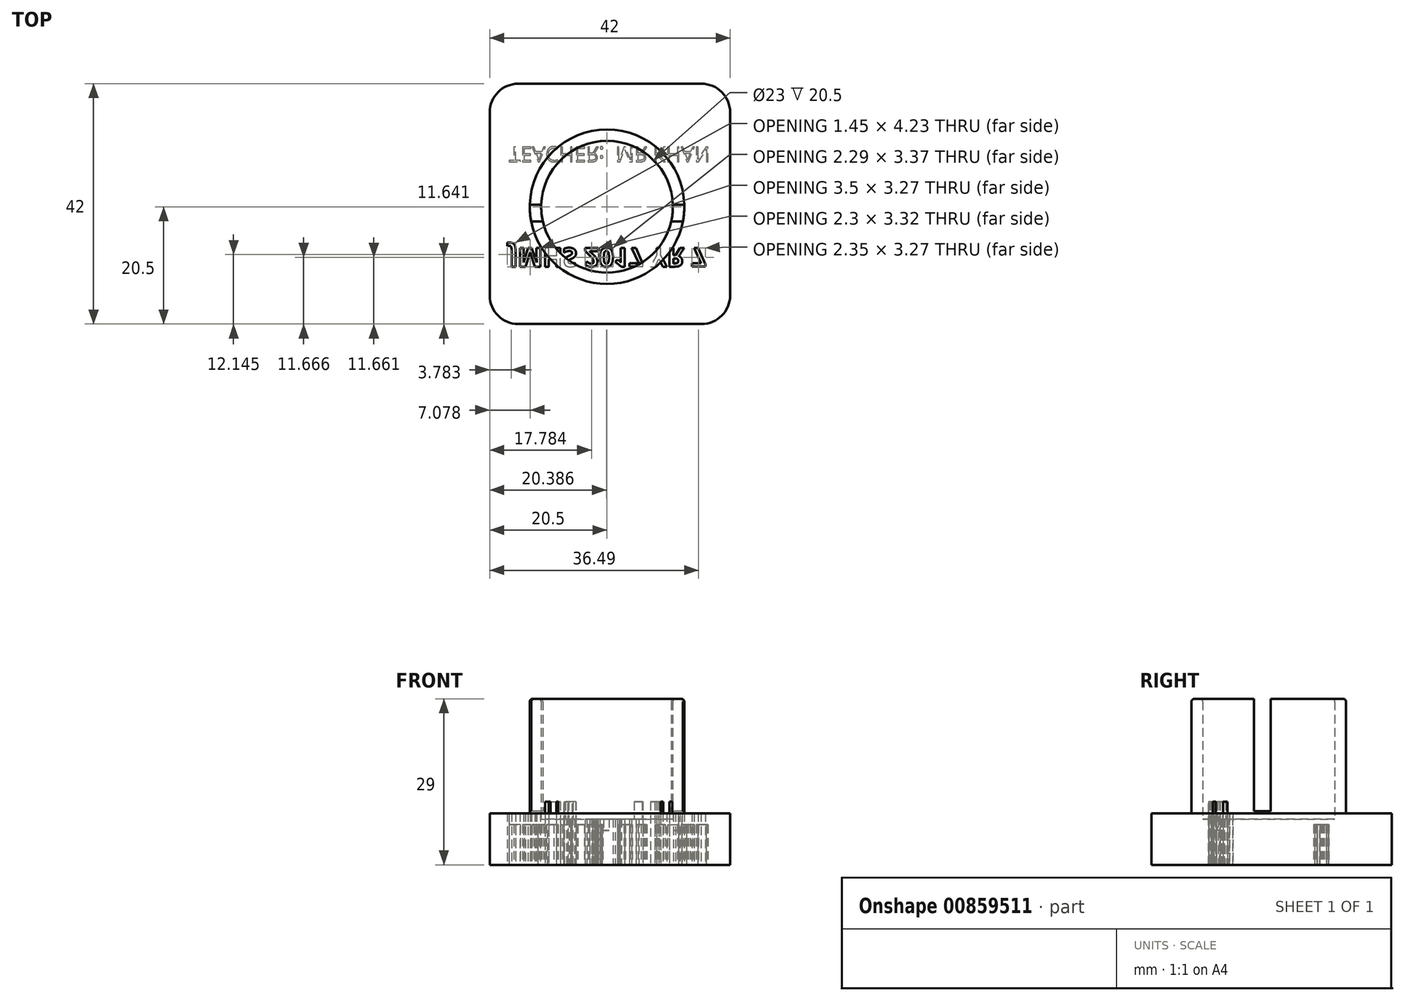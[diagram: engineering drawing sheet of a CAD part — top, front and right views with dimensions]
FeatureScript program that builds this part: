
annotation { "Feature Type Name" : "Feature", "Feature Type Description" : "" }
export const myFeature = defineFeature(function(context is Context, id is Id, definition is map)
    precondition{}
    {
        {
            var Q0;
            Q0=qCreatedBy(makeId("Top.planeOp"),FACE);
            var sketch = newSketch(context, id + "F0", { "sketchPlane" : qUnion([Q0])});
            skLineSegment(sketch, "E0.bottom", {"start": v(5, 0) * mm, "end": v(37, 0) * mm});
            skLineSegment(sketch, "E0.top", {"start": v(5, 42) * mm, "end": v(37, 42) * mm});
            skLineSegment(sketch, "E0.left", {"start": v(0, 5) * mm, "end": v(0, 37) * mm});
            skLineSegment(sketch, "E0.right", {"start": v(42, 5) * mm, "end": v(42, 37) * mm});
            skPoint(sketch, "E1.visualSharp", {"position": v(42, 42) * mm});
            skArc(sketch, "E1.filletArc", {"start": v(42, 37) * mm, "mid": v(40.54, 40.54) * mm, "end": v(37, 42) * mm});
            skPoint(sketch, "E2.visualSharp", {"position": v(42, 0) * mm});
            skArc(sketch, "E2.filletArc", {"start": v(37, 0) * mm, "mid": v(40.54, 1.46) * mm, "end": v(42, 5) * mm});
            skPoint(sketch, "E3.visualSharp", {"position": v(0, 42) * mm});
            skArc(sketch, "E3.filletArc", {"start": v(5, 42) * mm, "mid": v(1.46, 40.54) * mm, "end": v(0, 37) * mm});
            skPoint(sketch, "E4.visualSharp", {"position": v(0, 0) * mm});
            skArc(sketch, "E4.filletArc", {"start": v(0, 5) * mm, "mid": v(1.46, 1.46) * mm, "end": v(5, 0) * mm});
            skSolve(sketch);
        }
        {
            var Q0;
            Q0=makeQuery(id+"F0.imprint","IMPRINT",FACE,{"disambiguationData":[TD([[makeQuery(id+"F0.imprint","IMPRINT",EDGE,{"derivedFrom":sQuery(id+"F0.wireOp",EDGE,"E0.bottom")}),1.0]])]});
            extrude(context, id + "F1", {"entities" : qUnion([Q0]), "depth" : 3 * mm, "offsetDistance" : 25 * mm});
        }
        {
            var Q0;
            Q0=makeQuery(id+"F1.opExtrude","CAP_FACE",FACE,{"disambiguationData":[OSD([sQuery(id+"F0.wireOp",EDGE,"E0.bottom"),sQuery(id+"F0.wireOp",EDGE,"E0.top"),sQuery(id+"F0.wireOp",EDGE,"E0.left"),sQuery(id+"F0.wireOp",EDGE,"E0.right"),sQuery(id+"F0.wireOp",EDGE,"E1.filletArc"),sQuery(id+"F0.wireOp",EDGE,"E2.filletArc"),sQuery(id+"F0.wireOp",EDGE,"E3.filletArc"),sQuery(id+"F0.wireOp",EDGE,"E4.filletArc")])],"isStart":false});
            var sketch = newSketch(context, id + "F2", { "sketchPlane" : qUnion([Q0])});
            skCircle(sketch, "E5", {"center": v(20.5, 20.5) * mm, "radius": 13.5 * mm});
            skSolve(sketch);
        }
        {
            var Q0;
            Q0=makeQuery(id+"F2.imprint","IMPRINT",FACE,{"disambiguationData":[TD([[makeQuery(id+"F2.imprint","IMPRINT",EDGE,{"derivedFrom":sQuery(id+"F2.wireOp",EDGE,"E5")}),1.0]])]});
            extrude(context, id + "F3", {"entities" : qUnion([Q0]), "operationType" : NewBodyOperationType.ADD, "depth" : 20 * mm, "offsetDistance" : 25 * mm});
        }
        {
            var Q0;
            Q0=makeQuery(id+"F3.opExtrude","CAP_FACE",FACE,{"disambiguationData":[OSD([sQuery(id+"F2.wireOp",EDGE,"E5")])],"isStart":false});
            shell(context, id + "F4", {"entities" : qUnion([Q0]), "thickness" : 2 * mm});
        }
        {
            var Q0;
            {var subQ0=sQuery(id+"F2.wireOp",EDGE,"E5");Q0=makeQuery(id+"F4.opShell","OFFSET_EDGE",EDGE,{"disambiguationData":[OSD([subQ0]),TDD([makeQuery(id+"F3.opExtrude","CAP_EDGE",EDGE,{"disambiguationData":[OSD([subQ0])],"isStart":false})])]});}
            var Q1;
            Q1=makeQuery(id+"F3.opExtrude","CAP_EDGE",EDGE,{"disambiguationData":[OSD([sQuery(id+"F2.wireOp",EDGE,"E5")])],"isStart":false});
            fillet(context, id + "F5", {"entities" : qUnion([Q0, Q1]), "radius" : .5 * mm, "tangentPropagation" : true, "allowEdgeOverflow" : false});
        }
        {
            var Q0;
            Q0=makeQuery(id+"F1.opExtrude","CAP_FACE",FACE,{"disambiguationData":[OSD([sQuery(id+"F0.wireOp",EDGE,"E0.bottom"),sQuery(id+"F0.wireOp",EDGE,"E0.top"),sQuery(id+"F0.wireOp",EDGE,"E0.left"),sQuery(id+"F0.wireOp",EDGE,"E0.right"),sQuery(id+"F0.wireOp",EDGE,"E1.filletArc"),sQuery(id+"F0.wireOp",EDGE,"E2.filletArc"),sQuery(id+"F0.wireOp",EDGE,"E3.filletArc"),sQuery(id+"F0.wireOp",EDGE,"E4.filletArc")])],"isStart":true});
            var sketch = newSketch(context, id + "F6", { "sketchPlane" : qUnion([Q0])});
            skText(sketch, "E6", { "text": "JMHS 2017 YR 7", "fontName": "OpenSans-Bold.ttf"});
            const initialGuessF6  = {"E6": [0.0034, -0.0133, 1, 0, 0.0033]};
            skSetInitialGuess(sketch, initialGuessF6);
            skSolve(sketch);
        }
        {
            var Q0;
            Q0 = qSketchRegion(id + "F6", true);
            extrude(context, id + "F7", {"entities" : qUnion([Q0]), "operationType" : NewBodyOperationType.REMOVE, "oppositeDirection" : true, "depth" : 5 * mm, "offsetDistance" : 25 * mm});
        }
        {
            var Q0;
            Q0=qCreatedBy(makeId("Right.planeOp"),FACE);
            var sketch = newSketch(context, id + "F8", { "sketchPlane" : qUnion([Q0])});
            skLineSegment(sketch, "E7.bottom", {"start": v(20.85, 27.83) * mm, "end": v(17.94, 27.83) * mm});
            skLineSegment(sketch, "E7.top", {"start": v(20.85, 3.4) * mm, "end": v(17.94, 3.4) * mm});
            skLineSegment(sketch, "E7.left", {"start": v(20.85, 27.83) * mm, "end": v(20.85, 3.4) * mm});
            skLineSegment(sketch, "E7.right", {"start": v(17.94, 27.83) * mm, "end": v(17.94, 3.4) * mm});
            skSolve(sketch);
        }
        {
            var Q0;
            Q0 = qSketchRegion(id + "F8", true);
            extrude(context, id + "F9", {"entities" : qUnion([Q0]), "operationType" : NewBodyOperationType.REMOVE, "depth" : 61.5 * mm, "offsetDistance" : 25 * mm});
        }
        {
            var Q0;
            {var subQ0=sQuery(id+"F0.wireOp",EDGE,"E0.right");var subQ1=sQuery(id+"F0.wireOp",EDGE,"E0.left");var subQ2=sQuery(id+"F0.wireOp",EDGE,"E0.top");var subQ3=sQuery(id+"F0.wireOp",EDGE,"E1.filletArc");var subQ4=sQuery(id+"F0.wireOp",EDGE,"E2.filletArc");var subQ5=sQuery(id+"F0.wireOp",EDGE,"E3.filletArc");var subQ6=sQuery(id+"F0.wireOp",EDGE,"E4.filletArc");var subQ7=sQuery(id+"F0.wireOp",EDGE,"E0.bottom");Q0=makeQuery(id+"F7.boolean.opBoolean","SPLIT",FACE,{"disambiguationData":[TD([makeQuery(id+"F1.opExtrude","SWEPT_FACE",FACE,{"disambiguationData":[OSD([subQ7])]})])],"derivedFrom":makeQuery(id+"F1.opExtrude","CAP_FACE",FACE,{"disambiguationData":[OSD([subQ7,subQ2,subQ1,subQ0,subQ3,subQ4,subQ5,subQ6])],"isStart":true})});}
            extrude(context, id + "F10", {"entities" : qUnion([Q0]), "operationType" : NewBodyOperationType.ADD, "depth" : 6 * mm, "offsetDistance" : 25 * mm});
        }
        {
            var Q0;
            Q0=makeQuery(id+"F10.opExtrude","CAP_FACE",FACE,{"disambiguationData":[OSD([sQuery(id+"F0.wireOp",EDGE,"E0.bottom"),sQuery(id+"F0.wireOp",EDGE,"E0.top"),sQuery(id+"F0.wireOp",EDGE,"E0.left"),sQuery(id+"F0.wireOp",EDGE,"E0.right"),sQuery(id+"F0.wireOp",EDGE,"E1.filletArc"),sQuery(id+"F0.wireOp",EDGE,"E2.filletArc"),sQuery(id+"F0.wireOp",EDGE,"E3.filletArc"),sQuery(id+"F0.wireOp",EDGE,"E4.filletArc")])],"isStart":false});
            var sketch = newSketch(context, id + "F11", { "sketchPlane" : qUnion([Q0])});
            skText(sketch, "E8", { "text": "TEACHER:  MR KHAN ", "fontName": "OpenSans-Regular.ttf"});
            const initialGuessF11  = {"E8": [0.00335, -0.03098, 1, 0, 0.00264]};
            skSetInitialGuess(sketch, initialGuessF11);
            skSolve(sketch);
        }
        {
            var Q0;
            Q0 = qSketchRegion(id + "F11", true);
            extrude(context, id + "F12", {"entities" : qUnion([Q0]), "operationType" : NewBodyOperationType.REMOVE, "oppositeDirection" : true, "depth" : 7 * mm, "offsetDistance" : 25 * mm});
        }
    });
